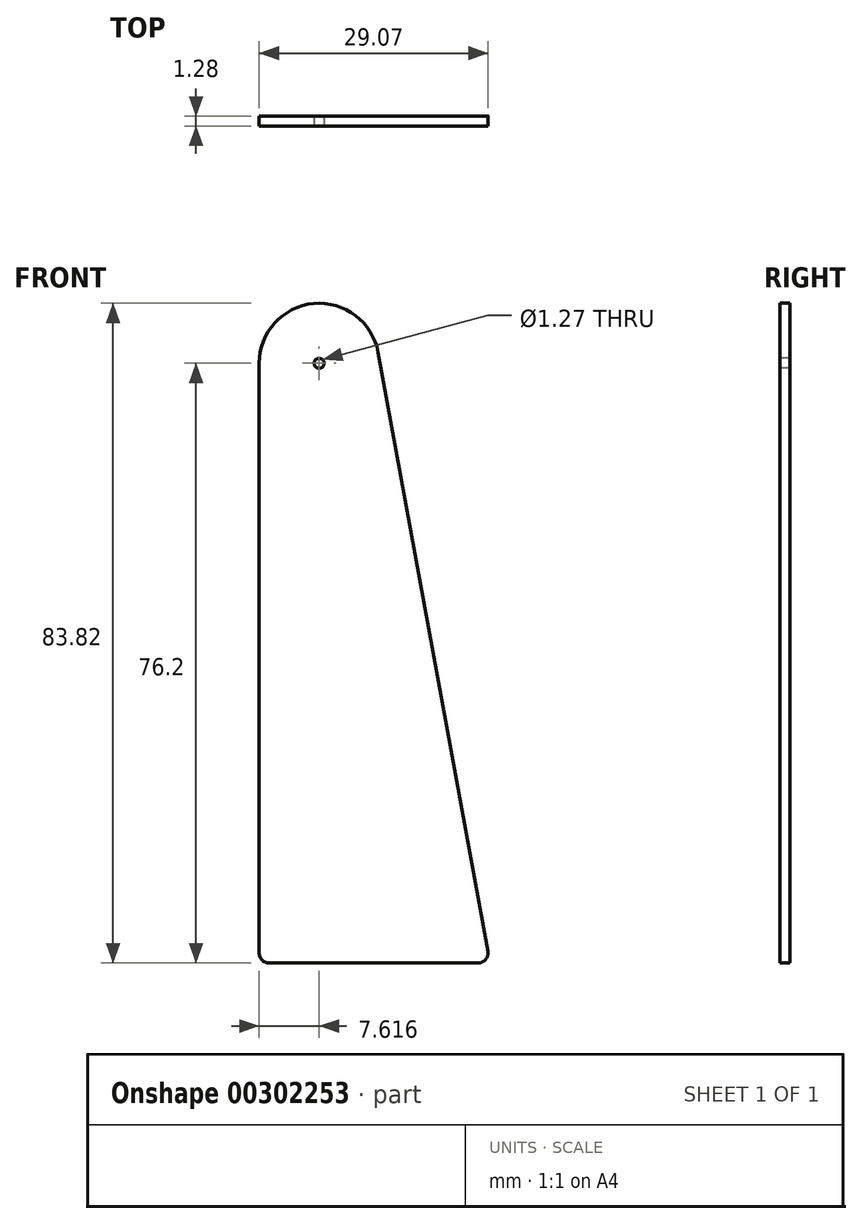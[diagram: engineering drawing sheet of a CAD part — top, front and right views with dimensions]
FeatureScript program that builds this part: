
annotation { "Feature Type Name" : "Feature", "Feature Type Description" : "" }
export const myFeature = defineFeature(function(context is Context, id is Id, definition is map)
    precondition{}
    {
        {
            var Q0;
            Q0=qCreatedBy(makeId("Front.planeOp"),FACE);
            var sketch = newSketch(context, id + "F0", { "sketchPlane" : qUnion([Q0])});
            skLineSegment(sketch, "E0", {"start": v(0, 0) * mm, "end": v(-29.32, 0) * mm});
            skLineSegment(sketch, "E1", {"start": v(-29.32, 0) * mm, "end": v(-29.32, 76.2) * mm});
            skLineSegment(sketch, "E2", {"start": v(0, 0) * mm, "end": v(-14.2, 77.57) * mm});
            skCircle(sketch, "E3", {"center": v(-21.7, 76.2) * mm, "radius": 7.62 * mm, "construction": true});
            skLineSegment(sketch, "E4", {"start": v(-21.7, 76.2) * mm, "end": v(-29.32, 76.2) * mm, "construction": true});
            skArc(sketch, "E5", {"start": v(-29.32, 76.2) * mm, "mid": v(-22.4, 83.79) * mm, "end": v(-14.2, 77.57) * mm});
            skSolve(sketch);
        }
        {
            var Q0;
            Q0 = qSketchRegion(id + "F0", true);
            extrude(context, id + "F1", {"entities" : qUnion([Q0]), "endBound" : BoundingType.SYMMETRIC, "depth" : 1.27 * mm});
        }
        {
            var Q0;
            Q0=makeQuery(id+"F1.opExtrude","CAP_FACE",FACE,{"disambiguationData":[OSD([sQuery(id+"F0.wireOp",EDGE,"E0"),sQuery(id+"F0.wireOp",EDGE,"E1"),sQuery(id+"F0.wireOp",EDGE,"E2"),sQuery(id+"F0.wireOp",EDGE,"E5")])],"isStart":false});
            var sketch = newSketch(context, id + "F2", { "sketchPlane" : qUnion([Q0])});
            skCircle(sketch, "E6", {"center": v(-21.7, 76.2) * mm, "radius": 0.64 * mm});
            skSolve(sketch);
        }
        {
            var Q0;
            Q0 = qSketchRegion(id + "F2", true);
            var Q1;
            Q1=makeQuery(id+"F1.opExtrude","CAP_FACE",FACE,{"disambiguationData":[OSD([sQuery(id+"F0.wireOp",EDGE,"E0"),sQuery(id+"F0.wireOp",EDGE,"E1"),sQuery(id+"F0.wireOp",EDGE,"E2"),sQuery(id+"F0.wireOp",EDGE,"E5")])],"isStart":true});
            extrude(context, id + "F3", {"entities" : qUnion([Q0]), "operationType" : NewBodyOperationType.REMOVE, "endBound" : BoundingType.UP_TO_SURFACE, "oppositeDirection" : true, "endBoundEntityFace" : qUnion([Q1]), "depth" : 25.4 * mm});
        }
        {
            var Q0;
            Q0=makeQuery(id+"F1.opExtrude","SWEPT_EDGE",EDGE,{"disambiguationData":[OSD([sQuery(id+"F0.wireOp",EDGE,"E0"),sQuery(id+"F0.wireOp",EDGE,"E1")])]});
            var Q1;
            Q1=makeQuery(id+"F1.opExtrude","SWEPT_EDGE",EDGE,{"disambiguationData":[OSD([sQuery(id+"F0.wireOp",EDGE,"E0"),sQuery(id+"F0.wireOp",EDGE,"E2")])]});
            fillet(context, id + "F4", {"entities" : qUnion([Q0, Q1]), "radius" : 1.27 * mm, "tangentPropagation" : true, "allowEdgeOverflow" : false});
        }
    });
